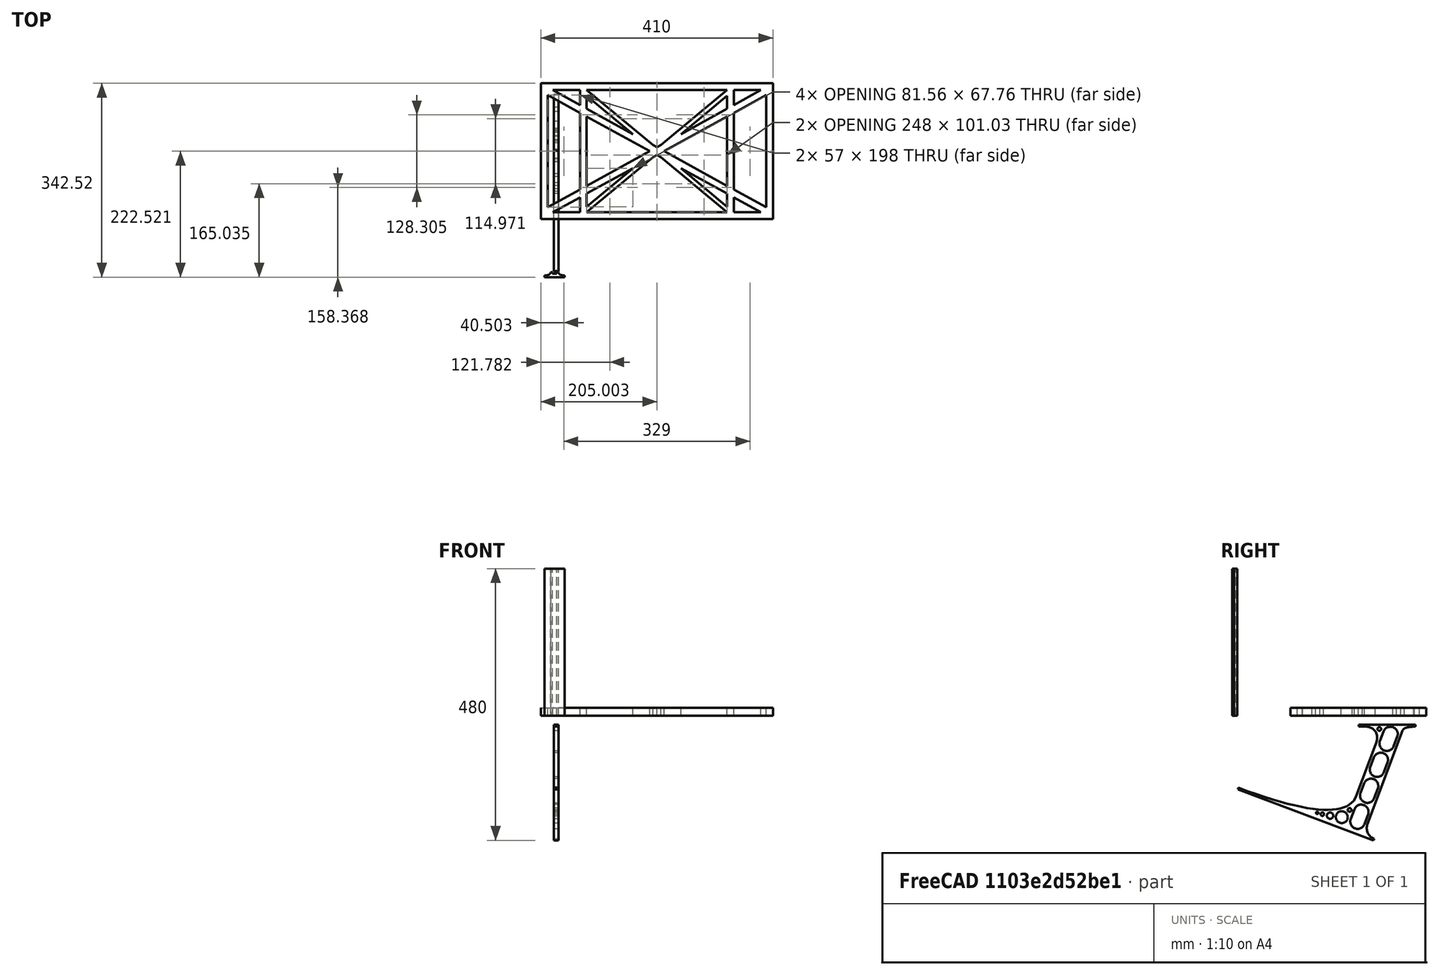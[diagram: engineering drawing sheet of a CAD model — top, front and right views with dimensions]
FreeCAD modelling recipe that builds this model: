
FCSTD DOCUMENT  (FreeCAD 0.19R0.19.2)
Label: laptopStand056
License: All rights reserved
LicenseURL: http://en.wikipedia.org/wiki/All_rights_reserved
objects: Sketcher::SketchObject×3, Part::Extrusion×3
note: 6 computed .brp shape members not serialized (recipe doc carries the construction recipe); baked Part::Feature solids carry a one-line shape summary decoded from their .brp

FEATURE [Sketcher::SketchObject] Sketch
  FullyConstrained = true
  sketch-geometry (102):
    g0: LineSegment StartX=-22.9272 StartY=136.221 StartZ=0 EndX=387.073 EndY=136.221 EndZ=0
    g1: LineSegment StartX=-22.9272 StartY=-103.779 StartZ=0 EndX=387.073 EndY=-103.779 EndZ=0
    g2: LineSegment StartX=375.073 StartY=115.221 StartZ=0 EndX=318.073 EndY=83.9235 EndZ=0
    g3: LineSegment StartX=-10.9272 StartY=-82.7794 StartZ=0 EndX=46.0728 EndY=-51.4823 EndZ=0
    g4: LineSegment StartX=-1.92718 StartY=124.221 StartZ=0 EndX=46.0728 EndY=97.8651 EndZ=0
    g5: LineSegment StartX=366.073 StartY=-91.7794 StartZ=0 EndX=318.073 EndY=-65.424 EndZ=0
    g6: LineSegment StartX=-10.9272 StartY=115.221 StartZ=0 EndX=-10.9272 EndY=-82.7794 EndZ=0
    g7: LineSegment StartX=375.073 StartY=-82.7794 StartZ=0 EndX=375.073 EndY=115.221 EndZ=0
    g8: LineSegment StartX=-1.92719 StartY=-91.7794 StartZ=0 EndX=46.0728 EndY=-91.7794 EndZ=0
    g9: LineSegment StartX=318.073 StartY=124.221 StartZ=0 EndX=366.073 EndY=124.221 EndZ=0
    g10: LineSegment StartX=306.073 StartY=-81.8102 StartZ=0 EndX=224.513 EndY=-14.0532 EndZ=0
    g11: LineSegment StartX=58.0728 StartY=114.251 StartZ=0 EndX=139.632 EndY=46.4944 EndZ=0
    g12: LineSegment StartX=306.073 StartY=124.221 StartZ=0 EndX=189.124 EndY=27.0628 EndZ=0
    g13: LineSegment StartX=58.0728 StartY=-91.7794 StartZ=0 EndX=175.022 EndY=5.37834 EndZ=0
    g14: LineSegment StartX=46.0728 StartY=124.221 StartZ=0 EndX=46.0728 EndY=97.8651 EndZ=0
    g15: LineSegment StartX=58.0728 StartY=-81.8102 StartZ=0 EndX=58.0728 EndY=-58.8351 EndZ=0
    g16: LineSegment StartX=318.073 StartY=124.221 StartZ=0 EndX=318.073 EndY=97.8651 EndZ=0
    g17: LineSegment StartX=306.073 StartY=114.251 StartZ=0 EndX=306.073 EndY=91.2763 EndZ=0
    g18: LineSegment StartX=224.513 StartY=46.4944 StartZ=0 EndX=306.073 EndY=114.251 EndZ=0
    g19: LineSegment StartX=175.022 StartY=27.0628 StartZ=0 EndX=58.0728 EndY=124.221 EndZ=0
    g20: LineSegment StartX=139.632 StartY=-14.0532 StartZ=0 EndX=58.0728 EndY=-81.8102 EndZ=0
    g21: LineSegment StartX=224.513 StartY=46.4944 StartZ=0 EndX=306.073 EndY=91.2763 EndZ=0
    g22: LineSegment StartX=139.632 StartY=-14.0532 StartZ=0 EndX=58.0728 EndY=-58.8351 EndZ=0
    g23: LineSegment StartX=189.124 StartY=5.37834 StartZ=0 EndX=306.073 EndY=-91.7794 EndZ=0
    g24: LineSegment StartX=306.073 StartY=77.3346 StartZ=0 EndX=306.073 EndY=-44.8935 EndZ=0
    g25: LineSegment StartX=318.073 StartY=83.9235 StartZ=0 EndX=318.073 EndY=-51.4823 EndZ=0
    g26: LineSegment StartX=318.073 StartY=97.8651 StartZ=0 EndX=366.073 EndY=124.221 EndZ=0
    g27: LineSegment StartX=306.073 StartY=-58.8351 StartZ=0 EndX=224.513 EndY=-14.0532 EndZ=0
    g28: LineSegment StartX=306.073 StartY=-58.8351 StartZ=0 EndX=306.073 EndY=-81.8102 EndZ=0
    g29: LineSegment StartX=318.073 StartY=-51.4823 StartZ=0 EndX=375.073 EndY=-82.7794 EndZ=0
    g30: LineSegment StartX=318.073 StartY=-65.424 StartZ=0 EndX=318.073 EndY=-91.7794 EndZ=0
    g31: LineSegment StartX=318.073 StartY=-91.7794 StartZ=0 EndX=366.073 EndY=-91.7794 EndZ=0
    g32: LineSegment StartX=58.0728 StartY=-44.8935 StartZ=0 EndX=58.0728 EndY=77.3346 EndZ=0
    g33: LineSegment StartX=46.0728 StartY=-65.424 StartZ=0 EndX=-1.92719 EndY=-91.7794 EndZ=0
    g34: LineSegment StartX=46.0728 StartY=-65.424 StartZ=0 EndX=46.0728 EndY=-91.7794 EndZ=0
    g35: LineSegment StartX=58.0728 StartY=91.2763 StartZ=0 EndX=58.0728 EndY=114.251 EndZ=0
    g36: LineSegment StartX=46.0728 StartY=83.9235 StartZ=0 EndX=46.0728 EndY=-51.4823 EndZ=0
    g37: LineSegment StartX=46.0728 StartY=124.221 StartZ=0 EndX=-1.92719 EndY=124.221 EndZ=0
    g38: LineSegment StartX=58.0728 StartY=91.2763 StartZ=0 EndX=139.632 EndY=46.4944 EndZ=0
    g39: LineSegment StartX=46.0728 StartY=83.9235 StartZ=0 EndX=-10.9272 EndY=115.221 EndZ=0
    g40: LineSegment StartX=-22.9272 StartY=136.221 StartZ=0 EndX=-42.9272 EndY=136.221 EndZ=0
    g41: LineSegment StartX=387.073 StartY=136.221 StartZ=0 EndX=407.073 EndY=136.221 EndZ=0
    g42: LineSegment StartX=-42.9272 StartY=136.221 StartZ=0 EndX=-42.9272 EndY=-103.779 EndZ=0
    g43: LineSegment StartX=-22.9272 StartY=-103.779 StartZ=0 EndX=-42.9272 EndY=-103.779 EndZ=0
    g44: LineSegment StartX=407.073 StartY=136.221 StartZ=0 EndX=407.073 EndY=-103.779 EndZ=0
    g45: LineSegment StartX=387.073 StartY=-103.779 StartZ=0 EndX=407.073 EndY=-103.779 EndZ=0
    g46: LineSegment StartX=179.022 StartY=27.0628 StartZ=0 EndX=179.022 EndY=124.221 EndZ=0
    g47: LineSegment StartX=185.124 StartY=27.0628 StartZ=0 EndX=185.124 EndY=124.221 EndZ=0
    g48: ArcOfCircle CenterX=-26.9272 CenterY=22.1087 CenterZ=0 NormalX=0 NormalY=0 NormalZ=1 AngleXU=0 Radius=8 StartAngle=1e-16 EndAngle=3.14159
    g49: ArcOfCircle CenterX=-26.9272 CenterY=-83.7794 CenterZ=0 NormalX=0 NormalY=0 NormalZ=1 AngleXU=0 Radius=8 StartAngle=3.14159 EndAngle=6.28319
    g50: LineSegment StartX=-34.9272 StartY=22.1087 StartZ=0 EndX=-34.9272 EndY=-83.7794 EndZ=0
    g51: LineSegment StartX=-18.9272 StartY=22.1087 StartZ=0 EndX=-18.9272 EndY=-83.7794 EndZ=0
    g52: LineSegment StartX=185.124 StartY=-91.7794 StartZ=0 EndX=306.073 EndY=-91.7794 EndZ=0
    g53: LineSegment StartX=179.022 StartY=-91.7794 StartZ=0 EndX=58.0728 EndY=-91.7794 EndZ=0
    g54: LineSegment StartX=306.073 StartY=124.221 StartZ=0 EndX=185.124 EndY=124.221 EndZ=0
    g55: LineSegment StartX=179.022 StartY=124.221 StartZ=0 EndX=58.0728 EndY=124.221 EndZ=0
    g56: ArcOfCircle CenterX=391.073 CenterY=22.1087 CenterZ=0 NormalX=0 NormalY=0 NormalZ=1 AngleXU=0 Radius=8 StartAngle=-4.4e-15 EndAngle=3.14159
    g57: LineSegment StartX=399.073 StartY=22.1087 StartZ=0 EndX=399.073 EndY=-83.7794 EndZ=0
    g58: LineSegment StartX=383.073 StartY=22.1087 StartZ=0 EndX=383.073 EndY=-83.7794 EndZ=0
    g59: ArcOfCircle CenterX=391.073 CenterY=-83.7794 CenterZ=0 NormalX=0 NormalY=0 NormalZ=1 AngleXU=0 Radius=8 StartAngle=3.14159 EndAngle=6.28319
    g60: Circle CenterX=175.022 CenterY=27.0628 CenterZ=0 NormalX=0 NormalY=0 NormalZ=1 AngleXU=0 Radius=1
    g61: Circle CenterX=179.022 CenterY=24.8665 CenterZ=0 NormalX=0 NormalY=0 NormalZ=1 AngleXU=0 Radius=1
    g62: Circle CenterX=179.022 CenterY=27.0628 CenterZ=0 NormalX=0 NormalY=0 NormalZ=1 AngleXU=0 Radius=1
    g63: BSplineCurve PolesCount=3 KnotsCount=2 Degree=2 IsPeriodic=0
    g64: GeomPoint X=175.022 Y=27.0628 Z=0
    g65: GeomPoint X=179.022 Y=27.0628 Z=0
    g66: Circle CenterX=189.124 CenterY=27.0628 CenterZ=0 NormalX=0 NormalY=0 NormalZ=1 AngleXU=0 Radius=1
    g67: Circle CenterX=185.124 CenterY=24.8665 CenterZ=0 NormalX=0 NormalY=0 NormalZ=1 AngleXU=0 Radius=1
    g68: Circle CenterX=185.124 CenterY=27.0628 CenterZ=0 NormalX=0 NormalY=0 NormalZ=1 AngleXU=0 Radius=1
    g69: BSplineCurve PolesCount=3 KnotsCount=2 Degree=2 IsPeriodic=0
    g70: GeomPoint X=189.124 Y=27.0628 Z=0
    g71: GeomPoint X=185.124 Y=27.0628 Z=0
    g72: Circle CenterX=175.022 CenterY=5.37834 CenterZ=0 NormalX=0 NormalY=0 NormalZ=1 AngleXU=0 Radius=1
    g73: Circle CenterX=179.022 CenterY=7.57463 CenterZ=0 NormalX=0 NormalY=0 NormalZ=1 AngleXU=0 Radius=1
    g74: Circle CenterX=179.022 CenterY=5.34704 CenterZ=0 NormalX=0 NormalY=0 NormalZ=1 AngleXU=0 Radius=1
    g75: BSplineCurve PolesCount=3 KnotsCount=2 Degree=2 IsPeriodic=0
    g76: GeomPoint X=175.022 Y=5.37834 Z=0
    g77: GeomPoint X=179.022 Y=5.34704 Z=0
    g78: Circle CenterX=189.124 CenterY=5.37834 CenterZ=0 NormalX=0 NormalY=0 NormalZ=1 AngleXU=0 Radius=1
    g79: Circle CenterX=185.124 CenterY=7.57463 CenterZ=0 NormalX=0 NormalY=0 NormalZ=1 AngleXU=0 Radius=1
    g80: Circle CenterX=185.124 CenterY=5.34704 CenterZ=0 NormalX=0 NormalY=0 NormalZ=1 AngleXU=0 Radius=1
    g81: BSplineCurve PolesCount=3 KnotsCount=2 Degree=2 IsPeriodic=0
    g82: GeomPoint X=189.124 Y=5.37834 Z=0
    g83: GeomPoint X=185.124 Y=5.34704 Z=0
    g84: LineSegment StartX=179.022 StartY=5.34704 StartZ=0 EndX=179.022 EndY=-91.7794 EndZ=0
    g85: LineSegment StartX=185.124 StartY=-91.7794 StartZ=0 EndX=185.124 EndY=5.34704 EndZ=0
    g86: Circle CenterX=165.871 CenterY=18.1458 CenterZ=0 NormalX=0 NormalY=0 NormalZ=1 AngleXU=0 Radius=1
    g87: Circle CenterX=169.377 CenterY=16.2206 CenterZ=0 NormalX=0 NormalY=0 NormalZ=1 AngleXU=0 Radius=1
    g88: Circle CenterX=165.871 CenterY=14.2954 CenterZ=0 NormalX=0 NormalY=0 NormalZ=1 AngleXU=0 Radius=1
    g89: BSplineCurve PolesCount=3 KnotsCount=2 Degree=2 IsPeriodic=0
    g90: GeomPoint X=165.871 Y=18.1458 Z=0
    g91: GeomPoint X=165.871 Y=14.2954 Z=0
    g92: Circle CenterX=198.275 CenterY=18.1458 CenterZ=0 NormalX=0 NormalY=0 NormalZ=1 AngleXU=0 Radius=1
    g93: Circle CenterX=194.768 CenterY=16.2206 CenterZ=0 NormalX=0 NormalY=0 NormalZ=1 AngleXU=0 Radius=1
    g94: Circle CenterX=198.275 CenterY=14.2954 CenterZ=0 NormalX=0 NormalY=0 NormalZ=1 AngleXU=0 Radius=1
    g95: BSplineCurve PolesCount=3 KnotsCount=2 Degree=2 IsPeriodic=0
    g96: GeomPoint X=198.275 Y=18.1458 Z=0
    g97: GeomPoint X=198.275 Y=14.2954 Z=0
    g98: LineSegment StartX=58.0728 StartY=77.3346 StartZ=0 EndX=165.871 EndY=18.1458 EndZ=0
    g99: LineSegment StartX=58.0728 StartY=-44.8935 StartZ=0 EndX=165.871 EndY=14.2954 EndZ=0
    g100: LineSegment StartX=198.275 StartY=18.1458 StartZ=0 EndX=306.073 EndY=77.3346 EndZ=0
    g101: LineSegment StartX=198.275 StartY=14.2954 StartZ=0 EndX=306.073 EndY=-44.8935 EndZ=0
  constraints (189):
    c: Horizontal(g0)
    c: Distance(g0) = 410
    c: Horizontal(g1)
    c: Block(g0)
    c: Horizontal(g8)
    c: Horizontal(g9)
    c: Coincident(g38,g11)
    c: Coincident(g18,g21)
    c: Coincident(g22,g20)
    c: Coincident(g27,g10)
    c: Coincident(g18,g17)
    c: Tangent(g17,g24)
    c: Tangent(g16,g25)
    c: Coincident(g21,g17)
    c: Tangent(g21,g26)
    c: Coincident(g2,g25)
    c: Coincident(g28,g10)
    c: Tangent(g5,g27)
    c: Tangent(g24,g28)
    c: Coincident(g25,g29)
    c: Coincident(g30,g5)
    c: Tangent(g25,g30)
    c: Coincident(g20,g15)
    c: Tangent(g15,g32)
    c: Coincident(g22,g15)
    c: Tangent(g22,g33)
    c: Coincident(g34,g33)
    c: Tangent(g14,g34)
    c: Coincident(g3,g36)
    c: Tangent(g32,g35)
    c: Tangent(g14,g36)
    c: Coincident(g11,g35)
    c: Coincident(g4,g14)
    c: Coincident(g38,g35)
    c: Tangent(g4,g38)
    c: Coincident(g39,g36)
    c: Block(g19)
    c: Block(g12)
    c: Block(g16)
    c: Block(g26)
    c: Block(g2)
    c: Block(g29)
    c: Block(g7)
    c: Block(g27)
    c: Block(g28)
    c: Block(g5)
    c: Block(g30)
    c: Block(g18)
    c: Block(g23)
    c: Block(g13)
    c: Block(g22)
    c: Block(g20)
    c: Block(g34)
    c: Block(g33)
    c: Block(g3)
    c: Block(g6)
    c: Block(g39)
    c: Block(g4)
    c: Block(g14)
    c: Block(g11)
    c: Block(g35)
    c: Block(g24)
    c: Block(g37)
    c: Block(g9)
    c: Block(g31)
    c: Block(g8)
    c: Horizontal(g40)
    c: Distance(g40) = 20
    c: Coincident(g41,g0)
    c: Horizontal(g41)
    c: Distance(g41) = 20
    c: Coincident(g42,g40)
    c: Vertical(g42)
    c: Horizontal(g43)
    c: Coincident(g43,g42)
    c: Coincident(g44,g41)
    c: Vertical(g44)
    c: Coincident(g45,g1)
    c: Horizontal(g45)
    c: Coincident(g45,g44)
    c: Block(g44)
    c: Block(g43)
    c: Block(g42)
    c: Block(g1)
    c: Vertical(g46)
    c: Vertical(g47)
    c: Block(g46)
    c: Block(g47)
    c: Tangent(g48,g51) = 1.5708
    c: Tangent(g48,g50) = -1.5708
    c: Tangent(g50,g49) = -1.5708
    c: Tangent(g51,g49) = 1.5708
    c: Vertical(g50)
    c: Equal(g48,g49)
    c: Block(g51)
    c: Block(g50)
    c: Coincident(g52,g23)
    c: Horizontal(g52)
    c: Coincident(g53,g13)
    c: Horizontal(g53)
    c: Coincident(g54,g12)
    c: Coincident(g54,g47)
    c: Horizontal(g54)
    c: Coincident(g55,g46)
    c: Coincident(g55,g19)
    c: Horizontal(g55)
    c: Distance(g45) = 20
    c: Distance(g1) = 410
    c: Tangent(g56,g57) = 1.5708
    c: Tangent(g57,g59) = 1.5708
    c: Equal(g56,g59)
    c: Coincident(g58,g56)
    c: Coincident(g58,g59)
    c: Block(g57)
    c: Block(g58)
    c: Coincident(g63,g19)
    c: Weight(g60) = 1
    c: Equal(g60,g61)
    c: Equal(g60,g62)
    c: Coincident(g63,g46)
    c: InternalAlignment(g60,g63)
    c: InternalAlignment(g61,g63)
    c: InternalAlignment(g62,g63)
    c: InternalAlignment(g64,g63)
    c: InternalAlignment(g65,g63)
    c: Coincident(g69,g12)
    c: Weight(g66) = 1
    c: Equal(g66,g67)
    c: Equal(g66,g68)
    c: Coincident(g69,g47)
    c: InternalAlignment(g66,g69)
    c: InternalAlignment(g67,g69)
    c: InternalAlignment(g68,g69)
    c: InternalAlignment(g70,g69)
    c: InternalAlignment(g71,g69)
    c: Block(g69)
    c: Block(g63)
    c: Coincident(g75,g13)
    c: Weight(g72) = 1
    c: Equal(g72,g73)
    c: Equal(g72,g74)
    c: InternalAlignment(g72,g75)
    c: InternalAlignment(g73,g75)
    c: InternalAlignment(g74,g75)
    c: InternalAlignment(g76,g75)
    c: InternalAlignment(g77,g75)
    c: Weight(g78) = 1
    c: Equal(g78,g79)
    c: Equal(g78,g80)
    c: InternalAlignment(g78,g81)
    c: InternalAlignment(g79,g81)
    c: InternalAlignment(g80,g81)
    c: InternalAlignment(g82,g81)
    c: InternalAlignment(g83,g81)
    c: Block(g81)
    c: Block(g75)
    c: Coincident(g84,g75)
    c: Coincident(g84,g53)
    c: Vertical(g84)
    c: Coincident(g85,g52)
    c: Coincident(g85,g81)
    c: Vertical(g85)
    c: Weight(g86) = 1
    c: Equal(g86,g87)
    c: Equal(g86,g88)
    c: InternalAlignment(g86,g89)
    c: InternalAlignment(g87,g89)
    c: InternalAlignment(g88,g89)
    c: InternalAlignment(g90,g89)
    c: InternalAlignment(g91,g89)
    c: Weight(g92) = 1
    c: Equal(g92,g93)
    c: Equal(g92,g94)
    c: InternalAlignment(g92,g95)
    c: InternalAlignment(g93,g95)
    c: InternalAlignment(g94,g95)
    c: InternalAlignment(g96,g95)
    c: InternalAlignment(g97,g95)
    c: Block(g95)
    c: Block(g89)
    c: Coincident(g98,g32)
    c: Coincident(g98,g89)
    c: Coincident(g99,g32)
    c: Coincident(g99,g89)
    c: Coincident(g100,g95)
    c: Coincident(g100,g24)
    c: Coincident(g101,g95)
    c: Coincident(g101,g24)
    c: Block(g32)
FEATURE [Sketcher::SketchObject] Sketch001
  FullyConstrained = true
  MapMode = 4
  Placement = pos=(0,0,0) rot=(0.57735,0.57735,0.57735;2.0944rad)
  Support = -> [Sketch]
  sketch-geometry (46):
    g0: BSplineCurve PolesCount=3 KnotsCount=2 Degree=2 IsPeriodic=0
    g1: ArcOfCircle CenterX=73.122 CenterY=-32.2909 CenterZ=0 NormalX=0 NormalY=0 NormalZ=1 AngleXU=0 Radius=13 StartAngle=5.92268 EndAngle=9.06428
    g2: ArcOfCircle CenterX=66.7816 CenterY=-49.1439 CenterZ=0 NormalX=0 NormalY=0 NormalZ=1 AngleXU=0 Radius=13 StartAngle=2.78068 EndAngle=5.92131
    g3: ArcOfCircle CenterX=55.9263 CenterY=-78.1807 CenterZ=0 NormalX=0 NormalY=0 NormalZ=1 AngleXU=0 Radius=13 StartAngle=5.92268 EndAngle=9.06428
    g4: ArcOfCircle CenterX=49.5884 CenterY=-95.0342 CenterZ=0 NormalX=0 NormalY=0 NormalZ=1 AngleXU=0 Radius=13 StartAngle=2.78068 EndAngle=5.92131
    g5: ArcOfCircle CenterX=38.7206 CenterY=-124.067 CenterZ=0 NormalX=0 NormalY=0 NormalZ=1 AngleXU=0 Radius=13 StartAngle=5.92268 EndAngle=9.06428
    g6: ArcOfCircle CenterX=32.3875 CenterY=-140.92 CenterZ=0 NormalX=0 NormalY=0 NormalZ=1 AngleXU=0 Radius=13 StartAngle=2.78068 EndAngle=5.92131
    g7: ArcOfCircle CenterX=21.4715 CenterY=-169.934 CenterZ=0 NormalX=0 NormalY=0 NormalZ=1 AngleXU=0 Radius=13 StartAngle=5.92268 EndAngle=9.06428
    g8: ArcOfCircle CenterX=15.1336 CenterY=-186.787 CenterZ=0 NormalX=0 NormalY=0 NormalZ=1 AngleXU=0 Radius=13 StartAngle=2.78068 EndAngle=5.92131
    g9-g12: Circle x4 (B-spline internal-alignment scaffolding for g13; pole/knot coordinates omitted)
    g13: BSplineCurve PolesCount=4 KnotsCount=2 Degree=3 IsPeriodic=0
    g14: GeomPoint X=28.8094 Y=-19.0875 Z=0
    g15: GeomPoint X=47.0443 Y=-50.4712 Z=0
    g16: Circle CenterX=53.5586 CenterY=-23.2695 CenterZ=0 NormalX=0 NormalY=0 NormalZ=1 AngleXU=0 Radius=3.24518
    g17: Circle CenterX=-195.441 CenterY=-127.082 CenterZ=0 NormalX=0 NormalY=0 NormalZ=1 AngleXU=0 Radius=1
    g18: Circle CenterX=-8.24091 CenterY=-197.481 CenterZ=0 NormalX=0 NormalY=0 NormalZ=1 AngleXU=0 Radius=1
    g19: Circle CenterX=12.8789 CenterY=-141.321 CenterZ=0 NormalX=0 NormalY=0 NormalZ=1 AngleXU=0 Radius=1
    g20: BSplineCurve PolesCount=3 KnotsCount=2 Degree=2 IsPeriodic=0
    g21: GeomPoint X=-195.441 Y=-127.082 Z=0
    g22: GeomPoint X=12.8789 Y=-141.321 Z=0
    g23: Circle CenterX=-12.8016 CenterY=-179.036 CenterZ=0 NormalX=0 NormalY=0 NormalZ=1 AngleXU=0 Radius=10.5072
    g24: Circle CenterX=0.933922 CenterY=-166.43 CenterZ=0 NormalX=0 NormalY=0 NormalZ=1 AngleXU=0 Radius=3.26661
    g25: Circle CenterX=-33.5518 CenterY=-176.44 CenterZ=0 NormalX=0 NormalY=0 NormalZ=1 AngleXU=0 Radius=5.64388
    g26: Circle CenterX=-47.2366 CenterY=-173.859 CenterZ=0 NormalX=0 NormalY=0 NormalZ=1 AngleXU=0 Radius=3.01653
    g27: Circle CenterX=-56.2595 CenterY=-171.456 CenterZ=0 NormalX=0 NormalY=0 NormalZ=1 AngleXU=0 Radius=2.12826
    g28: ArcOfCircle CenterX=51.2151 CenterY=-198.473 CenterZ=0 NormalX=0 NormalY=0 NormalZ=1 AngleXU=0 Radius=20 StartAngle=2.78189 EndAngle=4.35269
    g29: LineSegment StartX=32.4951 StartY=-191.433 StartZ=0 EndX=94.6577 EndY=-26.1351 EndZ=0
    g30: LineSegment StartX=43.1192 StartY=-220.001 StartZ=0 EndX=-196.497 EndY=-129.89 EndZ=0
    g31: LineSegment StartX=43.1192 StartY=-220.001 StartZ=0 EndX=44.1752 EndY=-217.193 EndZ=0
    g32: LineSegment StartX=117.223 StartY=-19.0875 StartZ=0 EndX=117.223 EndY=-16.0875 EndZ=0
    g33: LineSegment StartX=117.223 StartY=-16.0875 StartZ=0 EndX=17.2232 EndY=-16.0875 EndZ=0
    g34: LineSegment StartX=17.2232 StartY=-16.0875 StartZ=0 EndX=17.2232 EndY=-19.0875 EndZ=0
    g35: LineSegment StartX=28.8094 StartY=-19.0875 StartZ=0 EndX=17.2232 EndY=-19.0875 EndZ=0
    g36: LineSegment StartX=47.0443 StartY=-50.4712 StartZ=0 EndX=12.8789 EndY=-141.321 EndZ=0
    g37: LineSegment StartX=-195.441 StartY=-127.082 StartZ=0 EndX=-196.497 EndY=-129.89 EndZ=0
    g38: LineSegment StartX=85.2864 StartY=-36.8765 StartZ=0 EndX=78.9396 EndY=-53.7463 EndZ=0
    g39: LineSegment StartX=60.9577 StartY=-27.7052 StartZ=0 EndX=54.6191 EndY=-44.5532 EndZ=0
    g40: LineSegment StartX=68.0907 StartY=-82.7664 StartZ=0 EndX=61.7465 EndY=-99.6365 EndZ=0
    g41: LineSegment StartX=43.7619 StartY=-73.595 StartZ=0 EndX=37.426 EndY=-90.4435 EndZ=0
    g42: LineSegment StartX=50.885 StartY=-128.652 StartZ=0 EndX=44.5456 EndY=-145.522 EndZ=0
    g43: LineSegment StartX=26.5562 StartY=-119.481 StartZ=0 EndX=20.2251 EndY=-136.329 EndZ=0
    g44: LineSegment StartX=9.3071 StartY=-165.349 StartZ=0 EndX=2.97115 EndY=-182.197 EndZ=0
    g45: LineSegment StartX=33.6358 StartY=-174.52 StartZ=0 EndX=27.2917 EndY=-191.39 EndZ=0
  constraints (70):
    c: Block(g0)
    c: Block(g1)
    c: Block(g2)
    c: Block(g4)
    c: Block(g3)
    c: Block(g6)
    c: Block(g5)
    c: Block(g8)
    c: Block(g7)
    c: Weight(g9) = 1
    c: Equal(g9,g10)
    c: Equal(g9,g11)
    c: Equal(g9,g12)
    c: InternalAlignment(g9-g12 -> g13) x4
    c: InternalAlignment(g14,g13)
    c: InternalAlignment(g15,g13)
    c: Block(g16)
    c: Weight(g17) = 1
    c: Equal(g17,g18)
    c: Equal(g17,g19)
    c: InternalAlignment(g17,g20)
    c: InternalAlignment(g18,g20)
    c: InternalAlignment(g19,g20)
    c: InternalAlignment(g21,g20)
    c: InternalAlignment(g22,g20)
    c: Block(g20)
    c: Block(g23)
    c: Block(g24)
    c: Block(g25)
    c: Block(g26)
    c: Block(g27)
    c: Block(g28)
    c: Coincident(g29,g28)
    c: Coincident(g29,g0)
    c: Block(g13)
    c: Coincident(g31,g30)
    c: Coincident(g31,g28)
    c: Block(g31)
    c: Coincident(g32,g0)
    c: Vertical(g32)
    c: Coincident(g33,g32)
    c: Horizontal(g33)
    c: Coincident(g34,g33)
    c: Vertical(g34)
    c: Block(g33)
    c: Coincident(g35,g13)
    c: Coincident(g35,g34)
    c: Horizontal(g35)
    c: Coincident(g36,g13)
    c: Coincident(g36,g20)
    c: Coincident(g37,g20)
    c: Coincident(g37,g30)
    c: Block(g30)
    c: Coincident(g38,g1)
    c: Coincident(g38,g2)
    c: Coincident(g39,g1)
    c: Coincident(g39,g2)
    c: Coincident(g40,g3)
    c: Coincident(g40,g4)
    c: Coincident(g41,g3)
    c: Coincident(g41,g4)
    c: Coincident(g42,g5)
    c: Coincident(g42,g6)
    c: Coincident(g43,g5)
    c: Coincident(g43,g6)
    c: Coincident(g44,g7)
    c: Coincident(g44,g8)
    c: Coincident(g45,g7)
    c: Coincident(g45,g8)
    c: Distance(g30) = 256
FEATURE [Part::Extrusion] Extrude002
  Base = -> Sketch001
  Dir = (1,0,0)
  DirMode = 2
  FaceMakerClass = Part::FaceMakerBullseye
  LengthFwd = 8
  LengthRev = 0
  Solid = true
  Symmetric = false
FEATURE [Sketcher::SketchObject] Sketch002
  FullyConstrained = true
  sketch-geometry (20):
    g0: LineSegment StartX=-2.77179 StartY=-200.304 StartZ=0 EndX=5.22821 EndY=-200.304 EndZ=0
    g1: LineSegment StartX=5.22821 StartY=-200.304 StartZ=0 EndX=5.22821 EndY=-197.304 EndZ=0
    g2: LineSegment StartX=-2.77179 StartY=-200.304 StartZ=0 EndX=-2.77179 EndY=-197.304 EndZ=0
    g3: LineSegment StartX=5.22821 StartY=-197.304 StartZ=0 EndX=8.22821 EndY=-197.304 EndZ=0
    g4: LineSegment StartX=-2.77179 StartY=-197.304 StartZ=0 EndX=-5.77179 EndY=-197.304 EndZ=0
    g5: LineSegment StartX=19.2282 StartY=-203.304 StartZ=0 EndX=19.2282 EndY=-206.304 EndZ=0
    g6: LineSegment StartX=-16.7718 StartY=-203.304 StartZ=0 EndX=-16.7718 EndY=-206.304 EndZ=0
    g7: LineSegment StartX=-16.7718 StartY=-206.304 StartZ=0 EndX=19.2282 EndY=-206.304 EndZ=0
    g8: Circle CenterX=-16.7718 CenterY=-203.304 CenterZ=0 NormalX=0 NormalY=0 NormalZ=1 AngleXU=0 Radius=1
    g9: Circle CenterX=-5.77179 CenterY=-203.304 CenterZ=0 NormalX=0 NormalY=0 NormalZ=1 AngleXU=0 Radius=1
    g10: Circle CenterX=-5.77179 CenterY=-197.304 CenterZ=0 NormalX=0 NormalY=0 NormalZ=1 AngleXU=0 Radius=1
    g11: BSplineCurve PolesCount=3 KnotsCount=2 Degree=2 IsPeriodic=0
    g12: GeomPoint X=-16.7718 Y=-203.304 Z=0
    g13: GeomPoint X=-5.77179 Y=-197.304 Z=0
    g14: Circle CenterX=19.2282 CenterY=-203.304 CenterZ=0 NormalX=0 NormalY=0 NormalZ=1 AngleXU=0 Radius=1
    g15: Circle CenterX=8.22821 CenterY=-203.304 CenterZ=0 NormalX=0 NormalY=0 NormalZ=1 AngleXU=0 Radius=1
    g16: Circle CenterX=8.22821 CenterY=-197.304 CenterZ=0 NormalX=0 NormalY=0 NormalZ=1 AngleXU=0 Radius=1
    g17: BSplineCurve PolesCount=3 KnotsCount=2 Degree=2 IsPeriodic=0
    g18: GeomPoint X=19.2282 Y=-203.304 Z=0
    g19: GeomPoint X=8.22821 Y=-197.304 Z=0
  constraints (41):
    c: Horizontal(g0)
    c: Distance(g0) = 8
    c: Coincident(g1,g0)
    c: Vertical(g1)
    c: Distance(g1) = 3
    c: Coincident(g2,g0)
    c: Vertical(g2)
    c: Distance(g2) = 3
    c: Coincident(g3,g1)
    c: Horizontal(g3)
    c: Distance(g3) = 3
    c: Coincident(g4,g2)
    c: Horizontal(g4)
    c: Distance(g4) = 3
    c: Vertical(g5)
    c: Vertical(g6)
    c: Coincident(g7,g6)
    c: Coincident(g7,g5)
    c: Weight(g8) = 1
    c: Equal(g8,g9)
    c: Equal(g8,g10)
    c: Coincident(g11,g4)
    c: InternalAlignment(g8,g11)
    c: InternalAlignment(g9,g11)
    c: InternalAlignment(g10,g11)
    c: InternalAlignment(g12,g11)
    c: InternalAlignment(g13,g11)
    c: Coincident(g17,g5)
    c: Weight(g14) = 1
    c: Equal(g14,g15)
    c: Equal(g14,g16)
    c: Coincident(g17,g3)
    c: InternalAlignment(g14,g17)
    c: InternalAlignment(g15,g17)
    c: InternalAlignment(g16,g17)
    c: InternalAlignment(g18,g17)
    c: InternalAlignment(g19,g17)
    c: Block(g7)
    c: Block(g17)
    c: Block(g11)
    c: Block(g6)
FEATURE [Part::Extrusion] Extrude003
  Base = -> Sketch002
  Dir = (0,0,1)
  DirMode = 2
  FaceMakerClass = Part::FaceMakerBullseye
  LengthFwd = 260
  LengthRev = 0
  Solid = true
  Symmetric = false
FEATURE [Part::Extrusion] Extrude
  Base = -> Sketch
  Dir = (0,0,1)
  DirMode = 2
  FaceMakerClass = Part::FaceMakerBullseye
  LengthFwd = 14
  LengthRev = 0
  Solid = true
  Symmetric = false
